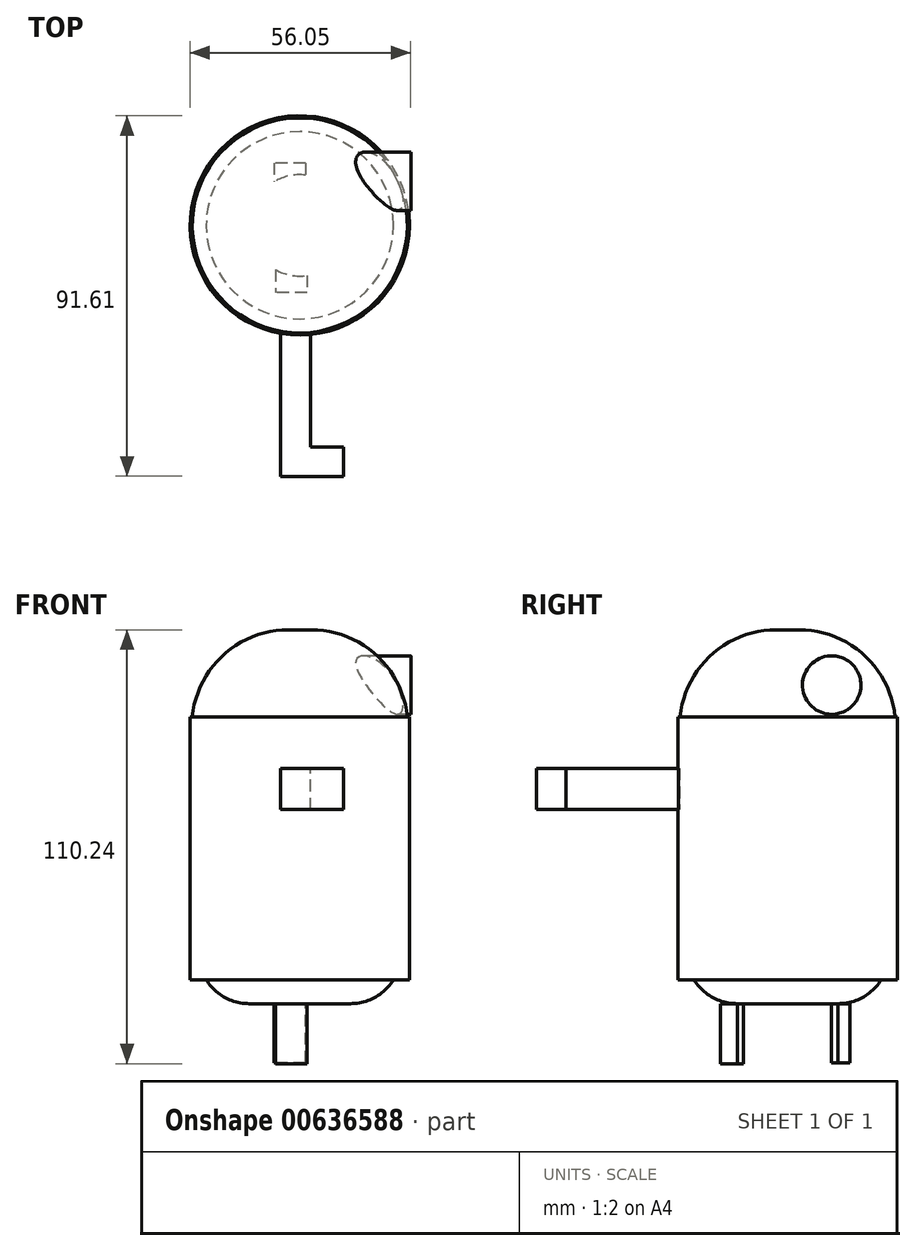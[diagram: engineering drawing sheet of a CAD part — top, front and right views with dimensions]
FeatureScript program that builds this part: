
annotation { "Feature Type Name" : "Feature", "Feature Type Description" : "" }
export const myFeature = defineFeature(function(context is Context, id is Id, definition is map)
    precondition{}
    {
        {
            var Q0;
            Q0=qCreatedBy(makeId("Top.planeOp"),FACE);
            var sketch = newSketch(context, id + "F0", { "sketchPlane" : qUnion([Q0])});
            skCircle(sketch, "E0", {"center": v(0, 0) * mm, "radius": 27.86 * mm});
            skSolve(sketch);
        }
        {
            var Q0;
            Q0=makeQuery(id+"F0.imprint","IMPRINT",FACE,{"disambiguationData":[TD([[makeQuery(id+"F0.imprint","IMPRINT",EDGE,{"derivedFrom":sQuery(id+"F0.wireOp",EDGE,"E0")}),1.0]])]});
            extrude(context, id + "F1", {"entities" : qUnion([Q0]), "depth" : 66.8 * mm, "offsetDistance" : 25.4 * mm});
        }
        {
            var Q0;
            Q0=makeQuery(id+"F1.opExtrude","CAP_FACE",FACE,{"disambiguationData":[OSD([sQuery(id+"F0.wireOp",EDGE,"E0")])],"isStart":false});
            var sketch = newSketch(context, id + "F2", { "sketchPlane" : qUnion([Q0])});
            skCircle(sketch, "E1", {"center": v(0, 0) * mm, "radius": 27.31 * mm});
            skSolve(sketch);
        }
        {
            var Q0;
            Q0=makeQuery(id+"F2.imprint","IMPRINT",FACE,{"disambiguationData":[TD([[makeQuery(id+"F2.imprint","IMPRINT",EDGE,{"derivedFrom":sQuery(id+"F2.wireOp",EDGE,"E1")}),1.0]])]});
            extrude(context, id + "F3", {"entities" : qUnion([Q0]), "operationType" : NewBodyOperationType.ADD, "depth" : 22.1 * mm, "offsetDistance" : 25.4 * mm});
        }
        {
            var Q0;
            Q0=makeQuery(id+"F3.opExtrude","CAP_FACE",FACE,{"disambiguationData":[OSD([sQuery(id+"F2.wireOp",EDGE,"E1")])],"isStart":false});
            fillet(context, id + "F4", {"entities" : qUnion([Q0]), "radius" : 24.53 * mm, "tangentPropagation" : true, "allowEdgeOverflow" : false});
        }
        {
            var Q0;
            Q0=makeQuery(id+"F1.opExtrude","CAP_FACE",FACE,{"disambiguationData":[OSD([sQuery(id+"F0.wireOp",EDGE,"E0")])],"isStart":true});
            var sketch = newSketch(context, id + "F5", { "sketchPlane" : qUnion([Q0])});
            skCircle(sketch, "E2", {"center": v(0, 0) * mm, "radius": 23.8 * mm});
            skSolve(sketch);
        }
        {
            var Q0;
            Q0=makeQuery(id+"F5.imprint","IMPRINT",FACE,{"disambiguationData":[TD([[makeQuery(id+"F5.imprint","IMPRINT",EDGE,{"derivedFrom":sQuery(id+"F5.wireOp",EDGE,"E2")}),1.0]])]});
            extrude(context, id + "F6", {"entities" : qUnion([Q0]), "operationType" : NewBodyOperationType.ADD, "depth" : 6.1 * mm, "offsetDistance" : 25.4 * mm});
        }
        {
            var Q0;
            Q0=makeQuery(id+"F6.opExtrude","CAP_EDGE",EDGE,{"disambiguationData":[OSD([sQuery(id+"F5.wireOp",EDGE,"E2")])],"isStart":false});
            fillet(context, id + "F7", {"entities" : qUnion([Q0]), "radius" : 12.88 * mm, "tangentPropagation" : true, "allowEdgeOverflow" : false});
        }
        {
            var Q0;
            Q0=makeQuery(id+"F6.opExtrude","CAP_FACE",FACE,{"disambiguationData":[OSD([sQuery(id+"F5.wireOp",EDGE,"E2")])],"isStart":false});
            var sketch = newSketch(context, id + "F8", { "sketchPlane" : qUnion([Q0])});
            skLineSegment(sketch, "E3.bottom", {"start": v(1.81, 9.3) * mm, "end": v(-6.15, 9.3) * mm});
            skLineSegment(sketch, "E3.top", {"start": v(1.81, 17.1) * mm, "end": v(-6.15, 17.1) * mm});
            skLineSegment(sketch, "E3.left", {"start": v(1.81, 9.3) * mm, "end": v(1.81, 17.1) * mm});
            skLineSegment(sketch, "E3.right", {"start": v(-6.15, 9.3) * mm, "end": v(-6.15, 17.1) * mm});
            skSolve(sketch);
        }
        {
            var Q0;
            {var subQ0=sQuery(id+"F8.wireOp",EDGE,"E3.top");Q0=makeQuery(id+"F8.imprint","IMPRINT",FACE,{"disambiguationData":[TD([[makeQuery(id+"F8.imprint","IMPRINT",EDGE,{"derivedFrom":subQ0}),1.0]])]});}
            extrude(context, id + "F9", {"entities" : qUnion([Q0]), "depth" : 15.24 * mm, "offsetDistance" : 25.4 * mm});
        }
        {
            var Q0;
            Q0=makeQuery(id+"F6.opExtrude","CAP_FACE",FACE,{"disambiguationData":[OSD([sQuery(id+"F5.wireOp",EDGE,"E2")])],"isStart":false});
            var sketch = newSketch(context, id + "F10", { "sketchPlane" : qUnion([Q0])});
            skLineSegment(sketch, "E4.bottom", {"start": v(1.42, -15.83) * mm, "end": v(-6.5, -15.83) * mm});
            skLineSegment(sketch, "E4.top", {"start": v(1.42, -11.09) * mm, "end": v(-6.5, -11.09) * mm});
            skLineSegment(sketch, "E4.left", {"start": v(1.42, -15.83) * mm, "end": v(1.42, -11.09) * mm});
            skLineSegment(sketch, "E4.right", {"start": v(-6.5, -15.83) * mm, "end": v(-6.5, -11.09) * mm});
            skSolve(sketch);
        }
        {
            var Q0;
            {var subQ0=sQuery(id+"F10.wireOp",EDGE,"E4.bottom");Q0=makeQuery(id+"F10.imprint","IMPRINT",FACE,{"disambiguationData":[TD([[makeQuery(id+"F10.imprint","IMPRINT",EDGE,{"derivedFrom":subQ0}),-1.0]])]});}
            extrude(context, id + "F11", {"entities" : qUnion([Q0]), "depth" : 15 * mm, "offsetDistance" : 25.4 * mm});
        }
        {
            var Q0;
            Q0=qCreatedBy(makeId("Right.planeOp"),FACE);
            var sketch = newSketch(context, id + "F12", { "sketchPlane" : qUnion([Q0])});
            skCircle(sketch, "E5", {"center": v(11.2, 74.85) * mm, "radius": 7.43 * mm});
            skSolve(sketch);
        }
        {
            var Q0;
            Q0=makeQuery(id+"F12.imprint","IMPRINT",FACE,{"disambiguationData":[TD([[makeQuery(id+"F12.imprint","IMPRINT",EDGE,{"derivedFrom":sQuery(id+"F12.wireOp",EDGE,"E5")}),1.0]])]});
            extrude(context, id + "F13", {"entities" : qUnion([Q0]), "operationType" : NewBodyOperationType.ADD, "depth" : 28.2 * mm, "offsetDistance" : 25.4 * mm});
        }
        {
            var Q0;
            Q0=qCreatedBy(makeId("Front.planeOp"),FACE);
            var sketch = newSketch(context, id + "F14", { "sketchPlane" : qUnion([Q0])});
            skLineSegment(sketch, "E6.bottom", {"start": v(2.77, 43.22) * mm, "end": v(-4.83, 43.22) * mm});
            skLineSegment(sketch, "E6.top", {"start": v(2.77, 53.7) * mm, "end": v(-4.83, 53.7) * mm});
            skLineSegment(sketch, "E6.left", {"start": v(2.77, 43.22) * mm, "end": v(2.77, 53.7) * mm});
            skLineSegment(sketch, "E6.right", {"start": v(-4.83, 43.22) * mm, "end": v(-4.83, 53.7) * mm});
            skSolve(sketch);
        }
        {
            var Q0;
            Q0=makeQuery(id+"F14.imprint","IMPRINT",FACE,{"disambiguationData":[TD([[makeQuery(id+"F14.imprint","IMPRINT",EDGE,{"derivedFrom":sQuery(id+"F14.wireOp",EDGE,"E6.bottom")}),-1.0]])]});
            extrude(context, id + "F15", {"entities" : qUnion([Q0]), "operationType" : NewBodyOperationType.ADD, "depth" : 63.75 * mm, "offsetDistance" : 25.4 * mm});
        }
        {
            var Q0;
            Q0=makeQuery(id+"F15.opExtrude","SWEPT_FACE",FACE,{"disambiguationData":[OSD([sQuery(id+"F14.wireOp",EDGE,"E6.left")])]});
            var sketch = newSketch(context, id + "F16", { "sketchPlane" : qUnion([Q0])});
            skLineSegment(sketch, "E7.bottom", {"start": v(-56.3, 43.22) * mm, "end": v(-63.75, 43.22) * mm});
            skLineSegment(sketch, "E7.top", {"start": v(-56.3, 53.7) * mm, "end": v(-63.75, 53.7) * mm});
            skLineSegment(sketch, "E7.left", {"start": v(-56.3, 43.22) * mm, "end": v(-56.3, 53.7) * mm});
            skLineSegment(sketch, "E7.right", {"start": v(-63.75, 43.22) * mm, "end": v(-63.75, 53.7) * mm});
            skSolve(sketch);
        }
        {
            var Q0;
            Q0=makeQuery(id+"F16.imprint","IMPRINT",FACE,{"disambiguationData":[TD([[makeQuery(id+"F16.imprint","IMPRINT",EDGE,{"derivedFrom":sQuery(id+"F16.wireOp",EDGE,"E7.bottom")}),1.0]])]});
            extrude(context, id + "F17", {"entities" : qUnion([Q0]), "operationType" : NewBodyOperationType.ADD, "depth" : 8.38 * mm, "offsetDistance" : 25.4 * mm});
        }
    });
